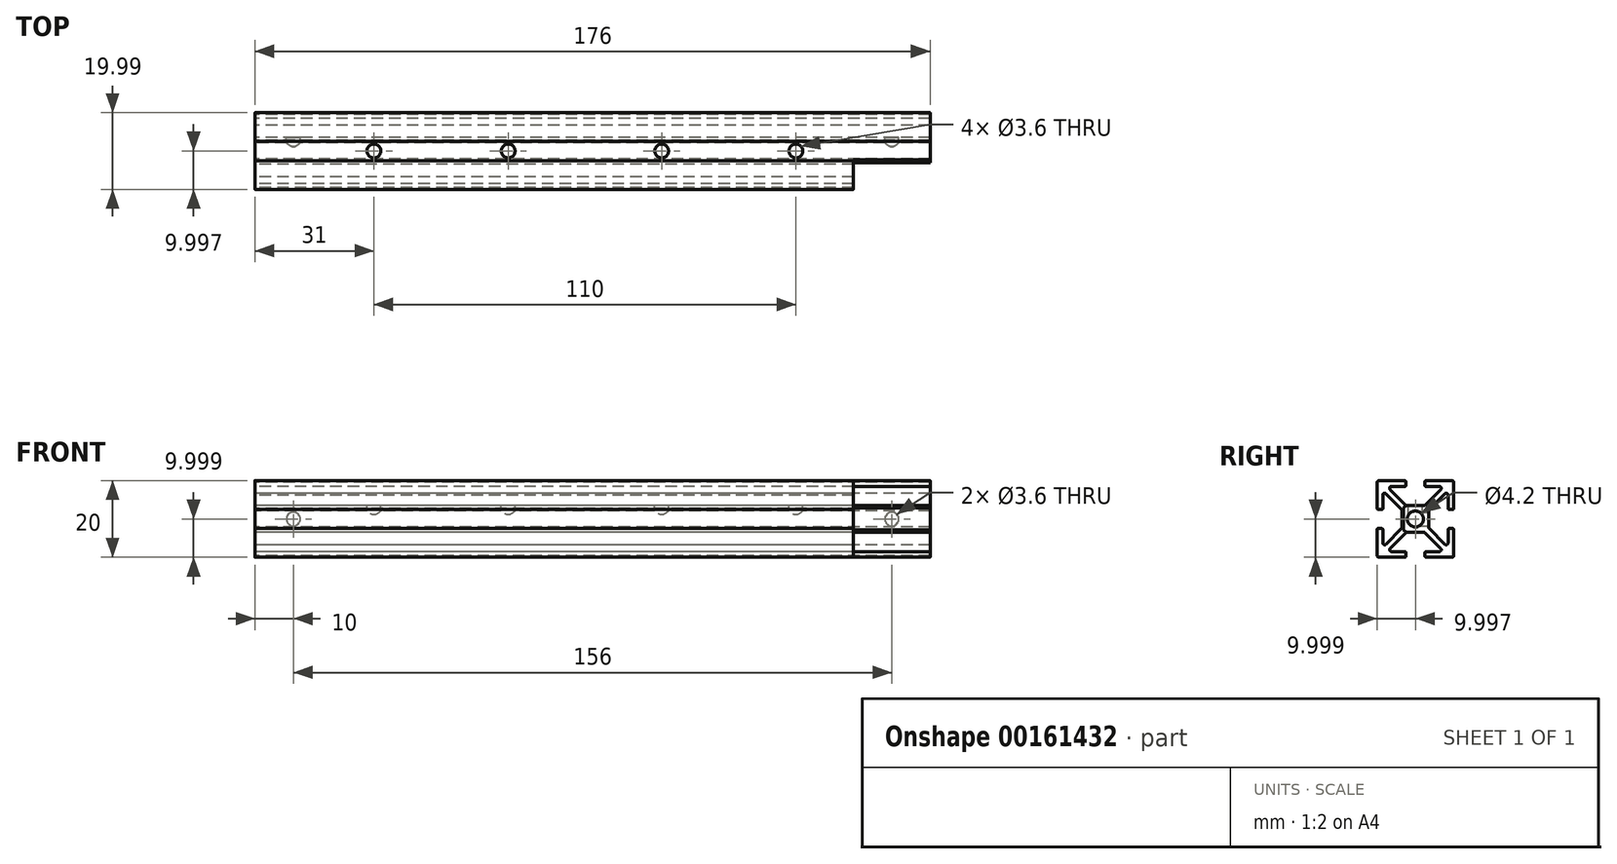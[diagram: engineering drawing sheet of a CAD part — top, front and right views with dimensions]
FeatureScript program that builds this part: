
annotation { "Feature Type Name" : "Feature", "Feature Type Description" : "" }
export const myFeature = defineFeature(function(context is Context, id is Id, definition is map)
    precondition{}
    {
        {
            var Q0;
            Q0=qCreatedBy(makeId("Right.planeOp"),FACE);
            var sketch = newSketch(context, id + "F0", { "sketchPlane" : qUnion([Q0])});
            skLineSegment(sketch, "E0.top", {"start": v(-10.52, -10.37) * mm, "end": v(-10.51, -10.37) * mm});
            skLineSegment(sketch, "E0.right", {"start": v(9.48, 9.63) * mm, "end": v(9.48, 9.63) * mm});
            skLineSegment(sketch, "E1.bottom", {"start": v(-3.26, 9.63) * mm, "end": v(-10.01, 9.63) * mm});
            skLineSegment(sketch, "E1.top", {"start": v(8.99, -10.37) * mm, "end": v(2.25, -10.37) * mm});
            skLineSegment(sketch, "E1.left", {"start": v(9.49, 9.13) * mm, "end": v(9.49, 2.38) * mm});
            skLineSegment(sketch, "E1.right", {"start": v(-10.51, -3.12) * mm, "end": v(-10.51, -9.87) * mm});
            skLineSegment(sketch, "E2", {"start": v(-10.51, 9.63) * mm, "end": v(-10.01, 9.13) * mm});
            skLineSegment(sketch, "E3", {"start": v(9.49, 9.63) * mm, "end": v(8.99, 9.13) * mm});
            skCircle(sketch, "E4", {"center": v(-0.51, -0.37) * mm, "radius": 2.1 * mm});
            skLineSegment(sketch, "E5.left", {"start": v(-3.01, 9.38) * mm, "end": v(-3.01, 8.38) * mm});
            skLineSegment(sketch, "E5.right", {"start": v(1.99, 9.38) * mm, "end": v(1.99, 8.38) * mm});
            skLineSegment(sketch, "E6", {"start": v(-4.01, 1.97) * mm, "end": v(-4.01, -2.7) * mm});
            skLineSegment(sketch, "E7", {"start": v(2.99, 1.97) * mm, "end": v(2.99, -2.7) * mm});
            skLineSegment(sketch, "E8", {"start": v(-6.75, -8.87) * mm, "end": v(-3.26, -8.87) * mm});
            skLineSegment(sketch, "E9", {"start": v(-9.01, -3.12) * mm, "end": v(-9.01, -6.6) * mm});
            skLineSegment(sketch, "E10", {"start": v(7.99, 5.86) * mm, "end": v(7.99, 2.38) * mm});
            skLineSegment(sketch, "E11", {"start": v(-6.75, 8.13) * mm, "end": v(-3.26, 8.13) * mm});
            skLineSegment(sketch, "E12.bottom", {"start": v(8.24, 2.13) * mm, "end": v(9.24, 2.13) * mm});
            skLineSegment(sketch, "E12.top", {"start": v(-10.26, -2.87) * mm, "end": v(-9.26, -2.87) * mm});
            skPoint(sketch, "E12.middle", {"position": v(9.49, -0.37) * mm});
            skLineSegment(sketch, "E13", {"start": v(-7.1, 7.28) * mm, "end": v(-3.03, 3.2) * mm});
            skLineSegment(sketch, "E14", {"start": v(2, -3.94) * mm, "end": v(6.07, -8.02) * mm});
            skLineSegment(sketch, "E15", {"start": v(6.07, 7.28) * mm, "end": v(2, 3.2) * mm});
            skLineSegment(sketch, "E16", {"start": v(-3.03, -3.94) * mm, "end": v(-7.1, -8.02) * mm});
            skArc(sketch, "E17.filletArc", {"start": v(-6.75, 8.13) * mm, "mid": v(-7.2, 7.82) * mm, "end": v(-7.1, 7.28) * mm});
            skPoint(sketch, "E18.newPointB", {"position": v(9.49, 8.13) * mm});
            skArc(sketch, "E18.filletArc", {"start": v(6.07, 7.28) * mm, "mid": v(6.18, 7.82) * mm, "end": v(5.72, 8.13) * mm});
            skArc(sketch, "E19.filletArc", {"start": v(7.99, 5.86) * mm, "mid": v(7.68, 6.32) * mm, "end": v(7.13, 6.22) * mm});
            skArc(sketch, "E20.filletArc", {"start": v(7.13, -6.96) * mm, "mid": v(7.68, -7.06) * mm, "end": v(7.99, -6.6) * mm});
            skArc(sketch, "E21.filletArc", {"start": v(5.72, -8.87) * mm, "mid": v(6.18, -8.56) * mm, "end": v(6.07, -8.02) * mm});
            skArc(sketch, "E22.filletArc", {"start": v(-7.1, -8.02) * mm, "mid": v(-7.2, -8.56) * mm, "end": v(-6.75, -8.87) * mm});
            skArc(sketch, "E23.filletArc", {"start": v(-9.01, -6.6) * mm, "mid": v(-8.7, -7.06) * mm, "end": v(-8.16, -6.96) * mm});
            skArc(sketch, "E24.filletArc", {"start": v(-8.16, 6.22) * mm, "mid": v(-8.73, 6.31) * mm, "end": v(-9, 5.8) * mm});
            skPoint(sketch, "E25.visualSharp", {"position": v(-10.51, 9.63) * mm});
            skArc(sketch, "E25.filletArc", {"start": v(-10.01, 9.63) * mm, "mid": v(-10.37, 9.48) * mm, "end": v(-10.51, 9.13) * mm});
            skPoint(sketch, "E26.visualSharp", {"position": v(9.49, 9.63) * mm});
            skArc(sketch, "E26.filletArc", {"start": v(9.49, 9.13) * mm, "mid": v(9.34, 9.48) * mm, "end": v(8.99, 9.63) * mm});
            skPoint(sketch, "E27.visualSharp", {"position": v(9.49, -10.37) * mm});
            skArc(sketch, "E27.filletArc", {"start": v(8.99, -10.37) * mm, "mid": v(9.34, -10.22) * mm, "end": v(9.49, -9.87) * mm});
            skPoint(sketch, "E28.visualSharp", {"position": v(-10.51, -10.37) * mm});
            skArc(sketch, "E28.filletArc", {"start": v(-10.51, -9.87) * mm, "mid": v(-10.37, -10.22) * mm, "end": v(-10.01, -10.37) * mm});
            skArc(sketch, "E29.filletArc", {"start": v(-3.26, 8.13) * mm, "mid": v(-3.09, 8.2) * mm, "end": v(-3.01, 8.38) * mm});
            skArc(sketch, "E30.filletArc", {"start": v(-9.01, -3.12) * mm, "mid": v(-9.09, -2.94) * mm, "end": v(-9.26, -2.87) * mm});
            skArc(sketch, "E31.filletArc", {"start": v(-3.01, 9.38) * mm, "mid": v(-3.09, 9.56) * mm, "end": v(-3.26, 9.63) * mm});
            skLineSegment(sketch, "E32", {"start": v(2.24, 9.63) * mm, "end": v(8.99, 9.63) * mm});
            skLineSegment(sketch, "E33", {"start": v(5.72, 8.13) * mm, "end": v(2.24, 8.13) * mm});
            skLineSegment(sketch, "E34", {"start": v(-9, 5.8) * mm, "end": v(-9, 2.38) * mm});
            skLineSegment(sketch, "E35", {"start": v(8.24, -2.87) * mm, "end": v(9.24, -2.87) * mm});
            skPoint(sketch, "E36.visualSharp", {"position": v(1.99, 8.13) * mm});
            skArc(sketch, "E36.filletArc", {"start": v(1.99, 8.38) * mm, "mid": v(2.06, 8.2) * mm, "end": v(2.24, 8.13) * mm});
            skPoint(sketch, "E37.visualSharp", {"position": v(1.99, 9.63) * mm});
            skArc(sketch, "E37.filletArc", {"start": v(2.24, 9.63) * mm, "mid": v(2.06, 9.56) * mm, "end": v(1.99, 9.38) * mm});
            skPoint(sketch, "E38.newPointB", {"position": v(-10.51, 2.13) * mm});
            skArc(sketch, "E38.filletArc", {"start": v(7.99, 2.38) * mm, "mid": v(8.06, 2.2) * mm, "end": v(8.24, 2.13) * mm});
            skLineSegment(sketch, "E39", {"start": v(7.99, -3.12) * mm, "end": v(7.99, -6.6) * mm});
            skPoint(sketch, "E40.visualSharp", {"position": v(7.99, -2.87) * mm});
            skArc(sketch, "E40.filletArc", {"start": v(8.24, -2.87) * mm, "mid": v(8.06, -2.94) * mm, "end": v(7.99, -3.12) * mm});
            skArc(sketch, "E41.filletArc", {"start": v(9.24, 2.13) * mm, "mid": v(9.41, 2.2) * mm, "end": v(9.49, 2.38) * mm});
            skLineSegment(sketch, "E42", {"start": v(9.49, -3.12) * mm, "end": v(9.49, -9.87) * mm});
            skPoint(sketch, "E43.visualSharp", {"position": v(9.49, -2.87) * mm});
            skArc(sketch, "E43.filletArc", {"start": v(9.49, -3.12) * mm, "mid": v(9.41, -2.94) * mm, "end": v(9.24, -2.87) * mm});
            skLineSegment(sketch, "E44", {"start": v(-9.26, 2.13) * mm, "end": v(-10.26, 2.13) * mm});
            skPoint(sketch, "E45.visualSharp", {"position": v(-9, 2.13) * mm});
            skArc(sketch, "E45.filletArc", {"start": v(-9.26, 2.13) * mm, "mid": v(-9.08, 2.2) * mm, "end": v(-9, 2.38) * mm});
            skPoint(sketch, "E46.newPointA", {"position": v(-10.51, -2.87) * mm});
            skArc(sketch, "E46.filletArc", {"start": v(-10.26, -2.87) * mm, "mid": v(-10.44, -2.94) * mm, "end": v(-10.51, -3.12) * mm});
            skLineSegment(sketch, "E47", {"start": v(-10.51, 2.38) * mm, "end": v(-10.51, 9.13) * mm});
            skArc(sketch, "E48.filletArc", {"start": v(-10.51, 2.38) * mm, "mid": v(-10.44, 2.2) * mm, "end": v(-10.26, 2.13) * mm});
            skPoint(sketch, "E49.newPointB", {"position": v(-3.01, 2.13) * mm});
            skLineSegment(sketch, "E50", {"start": v(7.13, -6.96) * mm, "end": v(3.06, -2.88) * mm});
            skPoint(sketch, "E50.endSnap0", {"position": v(2.99, -1.12) * mm});
            skPoint(sketch, "E51.newPointA", {"position": v(2.99, -2.8) * mm});
            skPoint(sketch, "E51.newPointB", {"position": v(2.99, -10.37) * mm});
            skArc(sketch, "E51.filletArc", {"start": v(2.99, -2.7) * mm, "mid": v(3, -2.8) * mm, "end": v(3.06, -2.88) * mm});
            skLineSegment(sketch, "E52", {"start": v(-2.85, -3.87) * mm, "end": v(1.82, -3.87) * mm});
            skArc(sketch, "E53.filletArc", {"start": v(2, -3.94) * mm, "mid": v(1.92, -3.89) * mm, "end": v(1.82, -3.87) * mm});
            skArc(sketch, "E54.filletArc", {"start": v(-2.85, -3.87) * mm, "mid": v(-2.94, -3.89) * mm, "end": v(-3.03, -3.94) * mm});
            skLineSegment(sketch, "E55", {"start": v(-8.16, -6.96) * mm, "end": v(-4.09, -2.88) * mm});
            skLineSegment(sketch, "E56", {"start": v(-8.16, 6.22) * mm, "end": v(-4.09, 2.14) * mm});
            skArc(sketch, "E57.filletArc", {"start": v(-4.01, 1.97) * mm, "mid": v(-4.03, 2.06) * mm, "end": v(-4.09, 2.14) * mm});
            skArc(sketch, "E58.filletArc", {"start": v(-4.09, -2.88) * mm, "mid": v(-4.03, -2.8) * mm, "end": v(-4.01, -2.7) * mm});
            skLineSegment(sketch, "E59", {"start": v(7.13, 6.22) * mm, "end": v(3.06, 2.14) * mm});
            skPoint(sketch, "E60.newPointB", {"position": v(2.99, 8.13) * mm});
            skArc(sketch, "E60.filletArc", {"start": v(3.06, 2.14) * mm, "mid": v(3, 2.06) * mm, "end": v(2.99, 1.97) * mm});
            skLineSegment(sketch, "E61", {"start": v(-2.85, 3.13) * mm, "end": v(1.82, 3.13) * mm});
            skArc(sketch, "E62.filletArc", {"start": v(-3.03, 3.2) * mm, "mid": v(-2.94, 3.15) * mm, "end": v(-2.85, 3.13) * mm});
            skArc(sketch, "E63.filletArc", {"start": v(1.82, 3.13) * mm, "mid": v(1.92, 3.15) * mm, "end": v(2, 3.2) * mm});
            skPoint(sketch, "E64.orphan", {"position": v(-3.01, 9.63) * mm});
            skPoint(sketch, "E65.orphan", {"position": v(-0.51, 9.63) * mm});
            skPoint(sketch, "E66.orphan", {"position": v(-10.51, -0.37) * mm});
            skLineSegment(sketch, "E67.trimOffspring", {"start": v(8.99, -9.87) * mm, "end": v(9.49, -10.37) * mm});
            skLineSegment(sketch, "E68.trimOffspring", {"start": v(-10.01, -9.87) * mm, "end": v(-10.51, -10.37) * mm});
            skPoint(sketch, "E69.trimOffspring.end.orphan", {"position": v(-0.51, -10.37) * mm});
            skLineSegment(sketch, "E70", {"start": v(2, 8.88) * mm, "end": v(2, 8.3) * mm});
            skPoint(sketch, "E70.startSnap0", {"position": v(1.99, 8.88) * mm});
            skLineSegment(sketch, "E71", {"start": v(-3.01, 8.88) * mm, "end": v(-3.01, 8.38) * mm});
            skPoint(sketch, "E72.start.orphan", {"position": v(-2.85, -8.87) * mm});
            skLineSegment(sketch, "E73.trimOffspring", {"start": v(2.25, -8.87) * mm, "end": v(5.72, -8.87) * mm});
            skLineSegment(sketch, "E74.trimOffspring", {"start": v(-3.26, -10.37) * mm, "end": v(-10.01, -10.37) * mm});
            skLineSegment(sketch, "E75.trimOffspring", {"start": v(2, -9.12) * mm, "end": v(2, -10.12) * mm});
            skLineSegment(sketch, "E76.trimOffspring", {"start": v(-3.01, -9.12) * mm, "end": v(-3.01, -10.12) * mm});
            skArc(sketch, "E77.filletArc", {"start": v(-3.01, -9.12) * mm, "mid": v(-3.09, -8.94) * mm, "end": v(-3.26, -8.87) * mm});
            skPoint(sketch, "E78.visualSharp", {"position": v(2, -8.87) * mm});
            skArc(sketch, "E78.filletArc", {"start": v(2.25, -8.87) * mm, "mid": v(2.07, -8.94) * mm, "end": v(2, -9.12) * mm});
            skPoint(sketch, "E79.visualSharp", {"position": v(-3.01, -10.37) * mm});
            skArc(sketch, "E79.filletArc", {"start": v(-3.26, -10.37) * mm, "mid": v(-3.09, -10.3) * mm, "end": v(-3.01, -10.12) * mm});
            skPoint(sketch, "E80.visualSharp", {"position": v(2, -10.37) * mm});
            skArc(sketch, "E80.filletArc", {"start": v(2, -10.12) * mm, "mid": v(2.07, -10.3) * mm, "end": v(2.25, -10.37) * mm});
            skLineSegment(sketch, "E81.trimOffspring", {"start": v(9.48, -3.08) * mm, "end": v(9.48, -9.93) * mm});
            skLineSegment(sketch, "E82.trimOffspring", {"start": v(2.24, -10.37) * mm, "end": v(9, -10.37) * mm});
            skLineSegment(sketch, "E83", {"start": v(-10.51, -9.87) * mm, "end": v(-10.51, -3.12) * mm});
            skLineSegment(sketch, "E84", {"start": v(-10.51, 9.13) * mm, "end": v(-10.51, 2.38) * mm});
            skLineSegment(sketch, "E85.trimOffspring", {"start": v(9.48, 9.19) * mm, "end": v(9.48, 2.34) * mm});
            skLineSegment(sketch, "E86.trimOffspring", {"start": v(9.48, -10.37) * mm, "end": v(9.48, -10.37) * mm});
            skLineSegment(sketch, "E87.trimOffspring", {"start": v(-10.03, -10.37) * mm, "end": v(-3.25, -10.37) * mm});
            skSolve(sketch);
        }
        {
            var Q0;
            Q0=makeQuery(id+"F0.imprint","IMPRINT",FACE,{"disambiguationData":[TD([[makeQuery(id+"F0.imprint","IMPRINT",EDGE,{"derivedFrom":sQuery(id+"F0.wireOp",EDGE,"E4")}),-1.0]])]});
            extrude(context, id + "F1", {"entities" : qUnion([Q0]), "depth" : 176 * mm});
        }
        {
            var Q0;
            Q0=makeQuery(id+"F1.opExtrude","CAP_FACE",FACE,{"disambiguationData":[OSD([sQuery(id+"F0.wireOp",EDGE,"E4"),sQuery(id+"F0.wireOp",EDGE,"E5.left"),sQuery(id+"F0.wireOp",EDGE,"E5.right"),sQuery(id+"F0.wireOp",EDGE,"E6"),sQuery(id+"F0.wireOp",EDGE,"E7"),sQuery(id+"F0.wireOp",EDGE,"E8"),sQuery(id+"F0.wireOp",EDGE,"E9"),sQuery(id+"F0.wireOp",EDGE,"E10"),sQuery(id+"F0.wireOp",EDGE,"E11"),sQuery(id+"F0.wireOp",EDGE,"E12.bottom"),sQuery(id+"F0.wireOp",EDGE,"E12.top"),sQuery(id+"F0.wireOp",EDGE,"E13"),sQuery(id+"F0.wireOp",EDGE,"E14"),sQuery(id+"F0.wireOp",EDGE,"E15"),sQuery(id+"F0.wireOp",EDGE,"E16"),sQuery(id+"F0.wireOp",EDGE,"E17.filletArc"),sQuery(id+"F0.wireOp",EDGE,"E18.filletArc"),sQuery(id+"F0.wireOp",EDGE,"E19.filletArc"),sQuery(id+"F0.wireOp",EDGE,"E20.filletArc"),sQuery(id+"F0.wireOp",EDGE,"E21.filletArc"),sQuery(id+"F0.wireOp",EDGE,"E22.filletArc"),sQuery(id+"F0.wireOp",EDGE,"E23.filletArc"),sQuery(id+"F0.wireOp",EDGE,"E24.filletArc"),sQuery(id+"F0.wireOp",EDGE,"E25.filletArc"),sQuery(id+"F0.wireOp",EDGE,"E26.filletArc"),sQuery(id+"F0.wireOp",EDGE,"E27.filletArc"),sQuery(id+"F0.wireOp",EDGE,"E28.filletArc"),sQuery(id+"F0.wireOp",EDGE,"E29.filletArc"),sQuery(id+"F0.wireOp",EDGE,"E30.filletArc"),sQuery(id+"F0.wireOp",EDGE,"E31.filletArc"),sQuery(id+"F0.wireOp",EDGE,"E33"),sQuery(id+"F0.wireOp",EDGE,"E34"),sQuery(id+"F0.wireOp",EDGE,"E35"),sQuery(id+"F0.wireOp",EDGE,"E36.filletArc"),sQuery(id+"F0.wireOp",EDGE,"E37.filletArc"),sQuery(id+"F0.wireOp",EDGE,"E38.filletArc"),sQuery(id+"F0.wireOp",EDGE,"E39"),sQuery(id+"F0.wireOp",EDGE,"E40.filletArc"),sQuery(id+"F0.wireOp",EDGE,"E41.filletArc"),sQuery(id+"F0.wireOp",EDGE,"E43.filletArc"),sQuery(id+"F0.wireOp",EDGE,"E44"),sQuery(id+"F0.wireOp",EDGE,"E45.filletArc"),sQuery(id+"F0.wireOp",EDGE,"E46.filletArc"),sQuery(id+"F0.wireOp",EDGE,"E48.filletArc"),sQuery(id+"F0.wireOp",EDGE,"E50"),sQuery(id+"F0.wireOp",EDGE,"E51.filletArc"),sQuery(id+"F0.wireOp",EDGE,"E52"),sQuery(id+"F0.wireOp",EDGE,"E53.filletArc"),sQuery(id+"F0.wireOp",EDGE,"E54.filletArc"),sQuery(id+"F0.wireOp",EDGE,"E55"),sQuery(id+"F0.wireOp",EDGE,"E56"),sQuery(id+"F0.wireOp",EDGE,"E57.filletArc"),sQuery(id+"F0.wireOp",EDGE,"E58.filletArc"),sQuery(id+"F0.wireOp",EDGE,"E59"),sQuery(id+"F0.wireOp",EDGE,"E60.filletArc"),sQuery(id+"F0.wireOp",EDGE,"E61"),sQuery(id+"F0.wireOp",EDGE,"E62.filletArc"),sQuery(id+"F0.wireOp",EDGE,"E63.filletArc"),sQuery(id+"F0.wireOp",EDGE,"E71"),sQuery(id+"F0.wireOp",EDGE,"E73.trimOffspring"),sQuery(id+"F0.wireOp",EDGE,"E75.trimOffspring"),sQuery(id+"F0.wireOp",EDGE,"E76.trimOffspring"),sQuery(id+"F0.wireOp",EDGE,"E77.filletArc"),sQuery(id+"F0.wireOp",EDGE,"E78.filletArc"),sQuery(id+"F0.wireOp",EDGE,"E79.filletArc"),sQuery(id+"F0.wireOp",EDGE,"E80.filletArc"),sQuery(id+"F0.wireOp",EDGE,"E81.trimOffspring"),sQuery(id+"F0.wireOp",EDGE,"E82.trimOffspring"),sQuery(id+"F0.wireOp",EDGE,"E83"),sQuery(id+"F0.wireOp",EDGE,"E84"),sQuery(id+"F0.wireOp",EDGE,"E32"),sQuery(id+"F0.wireOp",EDGE,"E1.bottom"),sQuery(id+"F0.wireOp",EDGE,"E85.trimOffspring"),sQuery(id+"F0.wireOp",EDGE,"E87.trimOffspring")])],"isStart":false});
            var sketch = newSketch(context, id + "F2", { "sketchPlane" : qUnion([Q0])});
            skLineSegment(sketch, "E88.bottom", {"start": v(-4.01, 9.63) * mm, "end": v(-10.51, 9.63) * mm});
            skLineSegment(sketch, "E88.top", {"start": v(-4.01, -10.37) * mm, "end": v(-10.51, -10.37) * mm});
            skLineSegment(sketch, "E88.right", {"start": v(-10.51, 9.63) * mm, "end": v(-10.51, -10.37) * mm});
            skLineSegment(sketch, "E89.bottom", {"start": v(-4.01, 9.63) * mm, "end": v(-3.01, 9.63) * mm});
            skLineSegment(sketch, "E89.top", {"start": v(-4.01, 8.13) * mm, "end": v(-3.01, 8.13) * mm});
            skLineSegment(sketch, "E89.right", {"start": v(-3.01, 9.63) * mm, "end": v(-3.01, 8.13) * mm});
            skLineSegment(sketch, "E90.bottom", {"start": v(-4.01, -8.87) * mm, "end": v(-3.01, -8.87) * mm});
            skLineSegment(sketch, "E90.top", {"start": v(-4.01, -10.37) * mm, "end": v(-3.01, -10.37) * mm});
            skLineSegment(sketch, "E90.right", {"start": v(-3.01, -8.87) * mm, "end": v(-3.01, -10.37) * mm});
            skLineSegment(sketch, "E91", {"start": v(-2.85, 3.13) * mm, "end": v(-3.58, 2.46) * mm});
            skPoint(sketch, "E91.endSnap0", {"position": v(-4.03, 2.06) * mm});
            skLineSegment(sketch, "E92", {"start": v(-2.85, -3.87) * mm, "end": v(-3.58, -3.14) * mm});
            skLineSegment(sketch, "E93", {"start": v(-2.85, -3.87) * mm, "end": v(-3.01, -8.87) * mm});
            skLineSegment(sketch, "E94", {"start": v(-3.01, 8.13) * mm, "end": v(-2.85, 3.13) * mm});
            skLineSegment(sketch, "E95", {"start": v(-3.58, 2.46) * mm, "end": v(-3.58, -3.14) * mm});
            skPoint(sketch, "E96.orphan", {"position": v(-4.01, 2.06) * mm});
            skSolve(sketch);
        }
        {
            var Q0;
            Q0 = qSketchRegion(id + "F2", true);
            extrude(context, id + "F3", {"entities" : qUnion([Q0]), "operationType" : NewBodyOperationType.REMOVE, "oppositeDirection" : true, "depth" : 20 * mm});
        }
        {
            var Q0;
            Q0=makeQuery(id+"F1.opExtrude","SWEPT_FACE",FACE,{"disambiguationData":[OSD([sQuery(id+"F0.wireOp",EDGE,"E7")])]});
            var sketch = newSketch(context, id + "F4", { "sketchPlane" : qUnion([Q0])});
            skPoint(sketch, "E97", {"position": v(-176, -0.37) * mm});
            skPoint(sketch, "E98", {"position": v(-166, -0.37) * mm});
            skCircle(sketch, "E99", {"center": v(-166, -0.37) * mm, "radius": 1.8 * mm});
            skPoint(sketch, "E100", {"position": v(-88, 1.97) * mm});
            skPoint(sketch, "E101", {"position": v(-10, -0.37) * mm});
            skCircle(sketch, "E102", {"center": v(-10, -0.37) * mm, "radius": 1.8 * mm});
            skSolve(sketch);
        }
        {
            var Q0;
            Q0 = qSketchRegion(id + "F4", true);
            extrude(context, id + "F5", {"entities" : qUnion([Q0]), "operationType" : NewBodyOperationType.REMOVE, "oppositeDirection" : true, "depth" : 3 * mm});
        }
        {
            var Q0;
            Q0=makeQuery(id+"F1.opExtrude","SWEPT_FACE",FACE,{"disambiguationData":[OSD([sQuery(id+"F0.wireOp",EDGE,"E61")])]});
            var sketch = newSketch(context, id + "F6", { "sketchPlane" : qUnion([Q0])});
            skLineSegment(sketch, "E103", {"start": v(176, -0.51) * mm, "end": v(-4.8, -0.51) * mm});
            skPoint(sketch, "E103.endSnap0", {"position": v(0, -0.51) * mm});
            skPoint(sketch, "E104", {"position": v(141, -0.51) * mm});
            skPoint(sketch, "E105", {"position": v(106, -0.51) * mm});
            skPoint(sketch, "E106", {"position": v(66, -0.51) * mm});
            skPoint(sketch, "E107", {"position": v(31, -0.51) * mm});
            skCircle(sketch, "E108", {"center": v(141, -0.51) * mm, "radius": 1.8 * mm});
            skCircle(sketch, "E109", {"center": v(106, -0.51) * mm, "radius": 1.8 * mm});
            skCircle(sketch, "E110", {"center": v(66, -0.51) * mm, "radius": 1.8 * mm});
            skCircle(sketch, "E111", {"center": v(31, -0.51) * mm, "radius": 1.8 * mm});
            skSolve(sketch);
        }
        {
            var Q0;
            Q0 = qSketchRegion(id + "F6", true);
            extrude(context, id + "F7", {"entities" : qUnion([Q0]), "operationType" : NewBodyOperationType.REMOVE, "oppositeDirection" : true, "depth" : 3 * mm});
        }
    });
